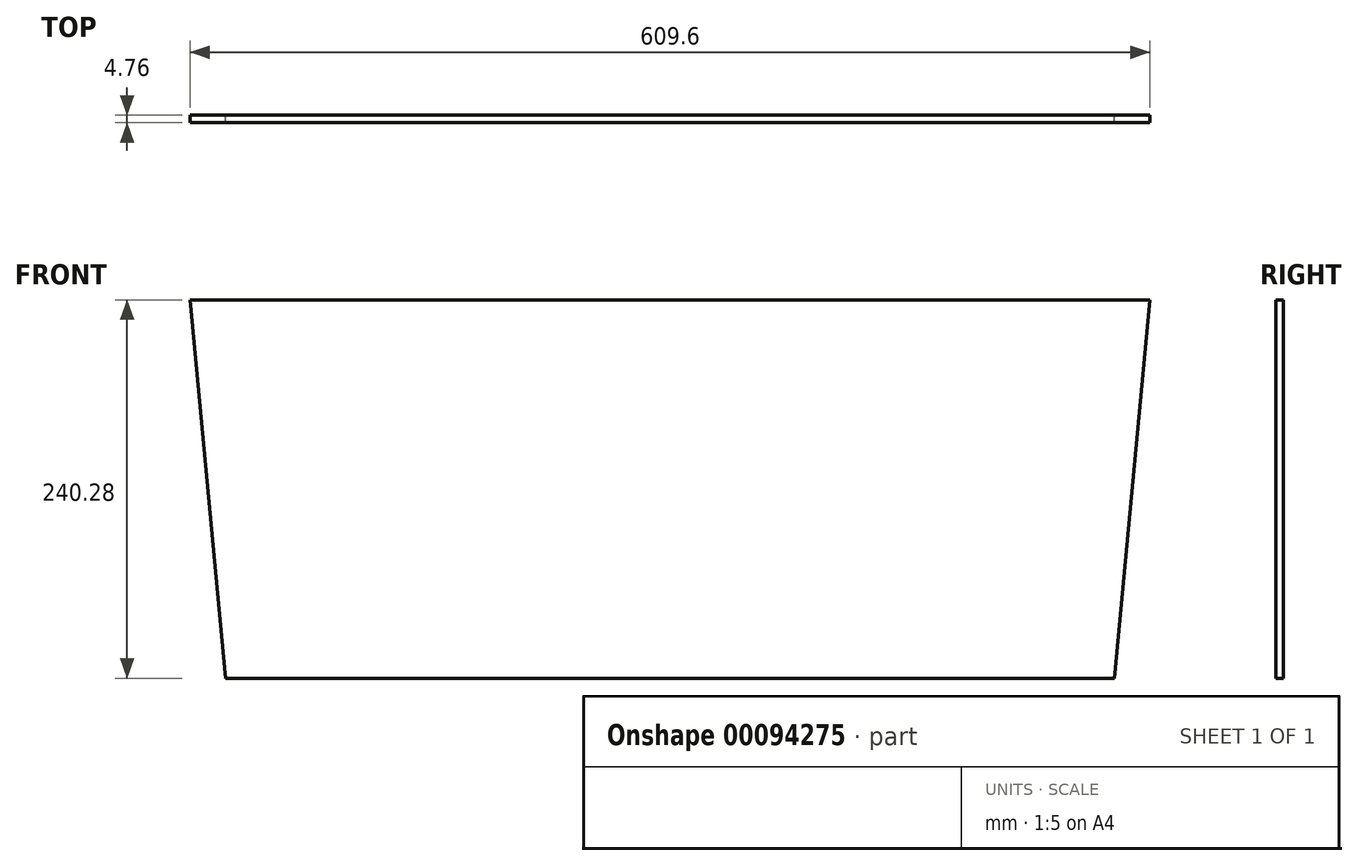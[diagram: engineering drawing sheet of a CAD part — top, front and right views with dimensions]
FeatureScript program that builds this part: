
annotation { "Feature Type Name" : "Feature", "Feature Type Description" : "" }
export const myFeature = defineFeature(function(context is Context, id is Id, definition is map)
    precondition{}
    {
        {
            var Q0;
            Q0=qCreatedBy(makeId("Front.planeOp"),FACE);
            var sketch = newSketch(context, id + "F0", { "sketchPlane" : qUnion([Q0])});
            skPoint(sketch, "E0.middle", {"position": v(-7.59, 0) * mm});
            skPoint(sketch, "E0.right.start.orphan", {"position": v(-428.82, 126.96) * mm});
            skPoint(sketch, "E0.left.start.orphan", {"position": v(413.64, 126.96) * mm});
            skPoint(sketch, "E0.top.end.orphan", {"position": v(-428.82, -126.96) * mm});
            skPoint(sketch, "E0.top.start.orphan", {"position": v(413.64, -126.96) * mm});
            skLineSegment(sketch, "E1.bottom", {"start": v(-316.63, 50.31) * mm, "end": v(292.97, 50.31) * mm});
            skLineSegment(sketch, "E1.top", {"start": v(-294.15, -189.97) * mm, "end": v(270.5, -189.97) * mm});
            skLineSegment(sketch, "E2", {"start": v(-316.63, 50.31) * mm, "end": v(-294.15, -189.97) * mm});
            skLineSegment(sketch, "E3", {"start": v(292.97, 50.31) * mm, "end": v(270.5, -189.97) * mm});
            skSolve(sketch);
        }
        {
            var Q0;
            Q0 = qSketchRegion(id + "F0", true);
            extrude(context, id + "F1", {"entities" : qUnion([Q0]), "depth" : 4.76 * mm});
        }
    });
